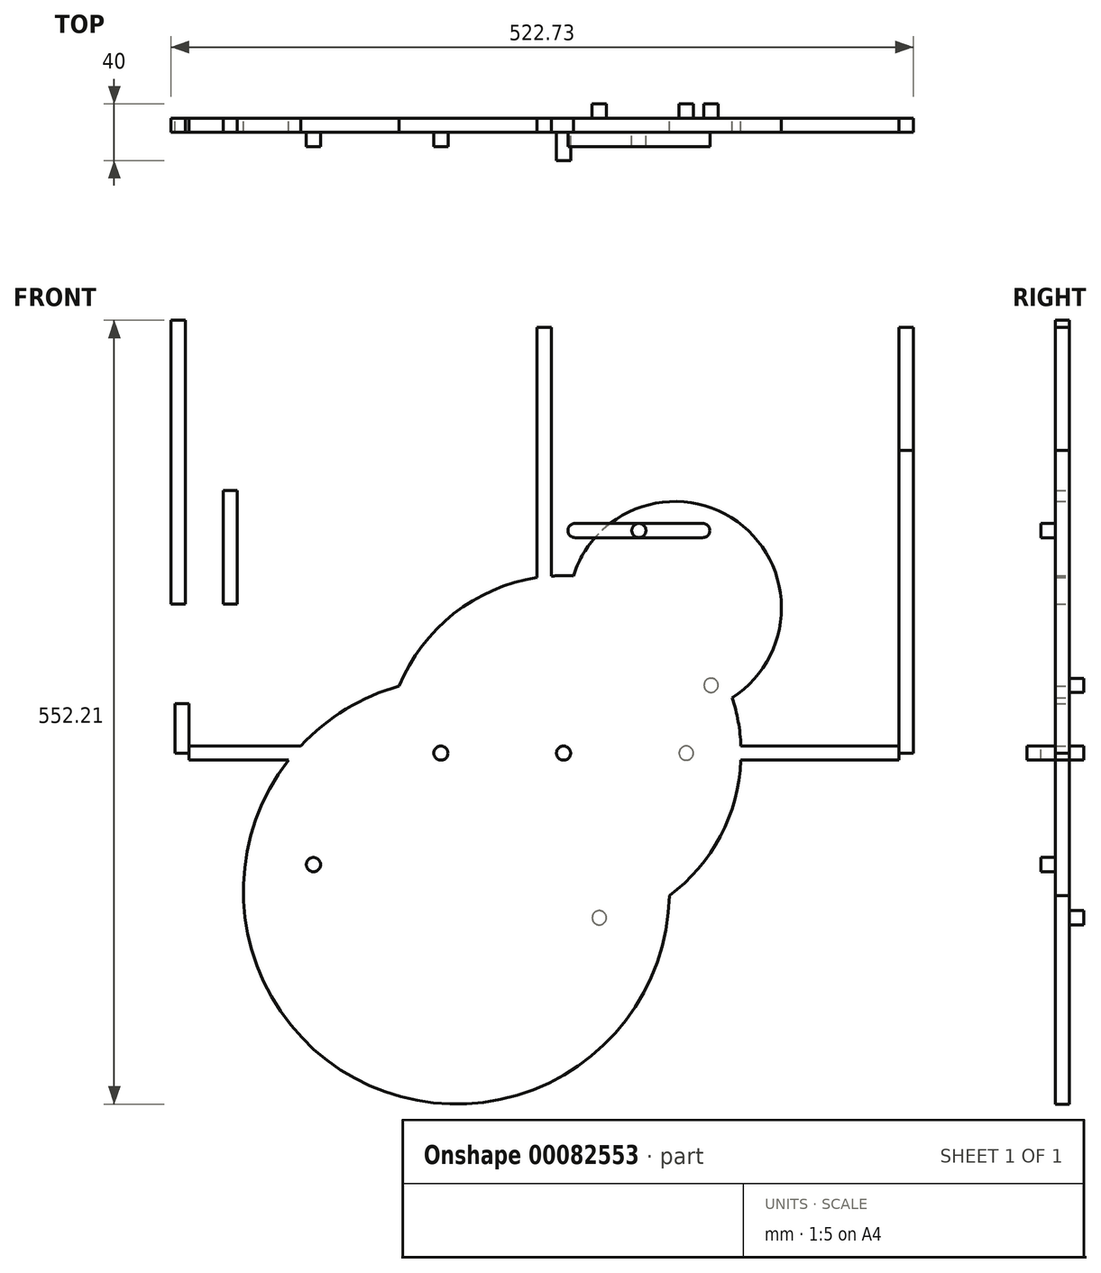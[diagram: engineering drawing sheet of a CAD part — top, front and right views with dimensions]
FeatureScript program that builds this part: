
annotation { "Feature Type Name" : "Feature", "Feature Type Description" : "" }
export const myFeature = defineFeature(function(context is Context, id is Id, definition is map)
    precondition{}
    {
        {
            var Q0;
            Q0=qCreatedBy(makeId("Front.planeOp"),FACE);
            var sketch = newSketch(context, id + "F0", { "sketchPlane" : qUnion([Q0])});
            skLineSegment(sketch, "E0", {"start": v(0, 0) * mm, "end": v(0, -300) * mm, "construction": true});
            skLineSegment(sketch, "E1", {"start": v(0, -300) * mm, "end": v(250, -300) * mm, "construction": true});
            skLineSegment(sketch, "E2", {"start": v(0, -300) * mm, "end": v(-250, -300) * mm, "construction": true});
            skLineSegment(sketch, "E3", {"start": v(0, 0) * mm, "end": v(5, 0) * mm});
            skLineSegment(sketch, "E4", {"start": v(5, 0) * mm, "end": v(5, -295) * mm});
            skLineSegment(sketch, "E5", {"start": v(5, -295) * mm, "end": v(250, -295) * mm});
            skLineSegment(sketch, "E6", {"start": v(250, -295) * mm, "end": v(250, -305) * mm});
            skLineSegment(sketch, "E7", {"start": v(250, -305) * mm, "end": v(-250, -305) * mm});
            skLineSegment(sketch, "E8", {"start": v(-250, -305) * mm, "end": v(-250, -295) * mm});
            skLineSegment(sketch, "E9", {"start": v(-250, -295) * mm, "end": v(-5, -295) * mm});
            skLineSegment(sketch, "E10", {"start": v(-5, -295) * mm, "end": v(-5, 0) * mm});
            skLineSegment(sketch, "E11", {"start": v(-5, 0) * mm, "end": v(0, 0) * mm});
            skSolve(sketch);
        }
        {
            var Q0;
            Q0 = qSketchRegion(id + "F0", true);
            extrude(context, id + "F1", {"entities" : qUnion([Q0]), "depth" : 10 * mm});
        }
        {
            var Q0;
            Q0=qCreatedBy(makeId("Front.planeOp"),FACE);
            var sketch = newSketch(context, id + "F2", { "sketchPlane" : qUnion([Q0])});
            skPoint(sketch, "E12.0", {"position": v(0, 0) * mm});
            skLineSegment(sketch, "E12.1", {"start": v(0, -300) * mm, "end": v(250, -300) * mm, "construction": true});
            skLineSegment(sketch, "E12.2", {"start": v(0, -300) * mm, "end": v(-250, -300) * mm, "construction": true});
            skLineSegment(sketch, "E13", {"start": v(0, 0) * mm, "end": v(0, 50) * mm, "construction": true});
            skLineSegment(sketch, "E14", {"start": v(0, 0) * mm, "end": v(-25.88, 96.6) * mm, "construction": true});
            skLineSegment(sketch, "E15", {"start": v(0, 0) * mm, "end": v(-100, 0) * mm, "construction": true});
            skLineSegment(sketch, "E16", {"start": v(0, 0) * mm, "end": v(-79.7, -6.97) * mm});
            skLineSegment(sketch, "E17", {"start": v(0, 0) * mm, "end": v(20.7, -77.27) * mm});
            skLineSegment(sketch, "E18", {"start": v(0, 0) * mm, "end": v(139.9, -300) * mm, "construction": true});
            skLineSegment(sketch, "E19", {"start": v(20.7, -77.27) * mm, "end": v(117.62, -252.23) * mm, "construction": true});
            skLineSegment(sketch, "E20", {"start": v(-79.7, -6.97) * mm, "end": v(66.76, -143.17) * mm, "construction": true});
            skLineSegment(sketch, "E21", {"start": v(66.76, -143.17) * mm, "end": v(117.62, -252.23) * mm});
            skCircle(sketch, "E22", {"center": v(92.19, -197.7) * mm, "radius": 75 * mm});
            skCircle(sketch, "E23", {"center": v(66.76, -143.17) * mm, "radius": 5 * mm});
            skLineSegment(sketch, "E24", {"start": v(-262.73, 4.92) * mm, "end": v(-262.73, -195.08) * mm});
            skLineSegment(sketch, "E25", {"start": v(-262.73, -195.08) * mm, "end": v(-252.73, -195.08) * mm});
            skLineSegment(sketch, "E26", {"start": v(-252.73, -195.08) * mm, "end": v(-252.73, 4.92) * mm});
            skLineSegment(sketch, "E27", {"start": v(-252.73, 4.92) * mm, "end": v(-262.73, 4.92) * mm});
            skLineSegment(sketch, "E28", {"start": v(92.19, -197.7) * mm, "end": v(87.19, -197.7) * mm});
            skLineSegment(sketch, "E29", {"start": v(87.19, -197.7) * mm, "end": v(87.19, -300) * mm});
            skLineSegment(sketch, "E30", {"start": v(87.19, -300) * mm, "end": v(97.19, -300) * mm});
            skLineSegment(sketch, "E31", {"start": v(97.19, -300) * mm, "end": v(97.19, -197.7) * mm});
            skLineSegment(sketch, "E32", {"start": v(97.19, -197.7) * mm, "end": v(92.19, -197.7) * mm});
            skLineSegment(sketch, "E33", {"start": v(-226.11, -195.08) * mm, "end": v(-226.11, -115.08) * mm});
            skLineSegment(sketch, "E34", {"start": v(-226.11, -115.08) * mm, "end": v(-216.11, -115.08) * mm});
            skLineSegment(sketch, "E35", {"start": v(-216.11, -115.08) * mm, "end": v(-216.11, -195.08) * mm});
            skLineSegment(sketch, "E36", {"start": v(-216.11, -195.08) * mm, "end": v(-226.11, -195.08) * mm});
            skLineSegment(sketch, "E37", {"start": v(97.19, -197.7) * mm, "end": v(132.22, -272.82) * mm});
            skLineSegment(sketch, "E38", {"start": v(132.22, -272.82) * mm, "end": v(128.11, -274.74) * mm});
            skLineSegment(sketch, "E39", {"start": v(124, -276.65) * mm, "end": v(97.19, -219.14) * mm});
            skLineSegment(sketch, "E40", {"start": v(124, -276.65) * mm, "end": v(124, -276.65) * mm});
            skLineSegment(sketch, "E41", {"start": v(128.11, -274.74) * mm, "end": v(124, -276.65) * mm});
            skSolve(sketch);
        }
        {
            var Q0;
            {var subQ1=sQuery(id+"F2.wireOp",EDGE,"E28");Q0=makeQuery(id+"F2.imprint","IMPRINT",FACE,{"disambiguationData":[TD([[makeQuery(id+"F2.imprint","IMPRINT",EDGE,{"derivedFrom":subQ1}),1.0]])]});}
            var Q1;
            {var subQ5=sQuery(id+"F2.wireOp",EDGE,"E30");Q1=makeQuery(id+"F2.imprint","IMPRINT",FACE,{"disambiguationData":[TD([[makeQuery(id+"F2.imprint","IMPRINT",EDGE,{"derivedFrom":subQ5}),1.0]])]});}
            var Q2;
            Q2=makeQuery(id+"F2.imprint","IMPRINT",FACE,{"disambiguationData":[TD([[makeQuery(id+"F2.imprint","IMPRINT",EDGE,{"derivedFrom":sQuery(id+"F2.wireOp",EDGE,"E33")}),-1.0]])]});
            var Q3;
            Q3=makeQuery(id+"F2.imprint","IMPRINT",FACE,{"disambiguationData":[TD([[makeQuery(id+"F2.imprint","IMPRINT",EDGE,{"derivedFrom":sQuery(id+"F2.wireOp",EDGE,"E24")}),1.0]])]});
            var Q4;
            {var subQ0=sQuery(id+"F2.wireOp",EDGE,"E32");Q4=makeQuery(id+"F2.imprint","IMPRINT",FACE,{"disambiguationData":[TD([[makeQuery(id+"F2.imprint","IMPRINT",EDGE,{"derivedFrom":subQ0}),1.0]])]});}
            var Q5;
            {var subQ3=sQuery(id+"F2.wireOp",EDGE,"E22");var subQ6=sQuery(id+"F2.wireOp",EDGE,"E39");var subQ8=makeQuery(id+"F2.imprint","INTERSECT",VERTEX,{"derivedFrom":[subQ3,subQ6]});Q5=makeQuery(id+"F2.imprint","IMPRINT",FACE,{"disambiguationData":[TD([[makeQuery(id+"F2.imprint","IMPRINT",EDGE,{"disambiguationData":[TD([[subQ8,-1.0]])],"derivedFrom":subQ3}),1.0]])]});}
            var Q6;
            {var subQ0=sQuery(id+"F2.wireOp",EDGE,"E38");Q6=makeQuery(id+"F2.imprint","IMPRINT",FACE,{"disambiguationData":[TD([[makeQuery(id+"F2.imprint","IMPRINT",EDGE,{"derivedFrom":subQ0}),-1.0]])]});}
            extrude(context, id + "F3", {"entities" : qUnion([Q0, Q1, Q2, Q3, Q4, Q5, Q6]), "operationType" : NewBodyOperationType.ADD, "depth" : 10 * mm});
        }
        {
            var Q0;
            {var subQ1=sQuery(id+"F2.wireOp",EDGE,"E28");Q0=makeQuery(id+"F2.imprint","IMPRINT",FACE,{"disambiguationData":[TD([[makeQuery(id+"F2.imprint","IMPRINT",EDGE,{"derivedFrom":subQ1}),1.0]])]});}
            var Q1;
            {var subQ0=sQuery(id+"F2.wireOp",EDGE,"E32");Q1=makeQuery(id+"F2.imprint","IMPRINT",FACE,{"disambiguationData":[TD([[makeQuery(id+"F2.imprint","IMPRINT",EDGE,{"derivedFrom":subQ0}),1.0]])]});}
            var Q2;
            Q2=makeQuery(id+"F2.imprint","IMPRINT",FACE,{"disambiguationData":[TD([[makeQuery(id+"F2.imprint","IMPRINT",EDGE,{"derivedFrom":sQuery(id+"F2.wireOp",EDGE,"E23")}),-1.0]])]});
            var Q3;
            {var subQ0=sQuery(id+"F2.wireOp",EDGE,"E31");var subQ1=sQuery(id+"F2.wireOp",EDGE,"E22");var subQ2=makeQuery(id+"F2.imprint","INTERSECT",VERTEX,{"derivedFrom":[subQ1,subQ0]});Q3=makeQuery(id+"F2.imprint","IMPRINT",FACE,{"disambiguationData":[TD([[makeQuery(id+"F2.imprint","IMPRINT",EDGE,{"disambiguationData":[TD([[subQ2,-1.0]])],"derivedFrom":subQ1}),1.0]])]});}
            var Q4;
            {var subQ3=sQuery(id+"F2.wireOp",EDGE,"E22");var subQ6=sQuery(id+"F2.wireOp",EDGE,"E39");var subQ8=makeQuery(id+"F2.imprint","INTERSECT",VERTEX,{"derivedFrom":[subQ3,subQ6]});Q4=makeQuery(id+"F2.imprint","IMPRINT",FACE,{"disambiguationData":[TD([[makeQuery(id+"F2.imprint","IMPRINT",EDGE,{"disambiguationData":[TD([[subQ8,-1.0]])],"derivedFrom":subQ3}),1.0]])]});}
            extrude(context, id + "F4", {"entities" : qUnion([Q0, Q1, Q2, Q3, Q4]), "depth" : 10 * mm});
        }
        {
            var Q0;
            Q0=makeQuery(id+"F2.imprint","IMPRINT",FACE,{"disambiguationData":[TD([[makeQuery(id+"F2.imprint","IMPRINT",EDGE,{"derivedFrom":sQuery(id+"F2.wireOp",EDGE,"E23")}),1.0]])]});
            extrude(context, id + "F5", {"entities" : qUnion([Q0]), "operationType" : NewBodyOperationType.ADD, "depth" : 20 * mm});
        }
        {
            var Q0;
            Q0=makeQuery(id+"F4.opExtrude","CAP_FACE",FACE,{"disambiguationData":[OSD([sQuery(id+"F2.wireOp",EDGE,"E22"),sQuery(id+"F2.wireOp",EDGE,"E23")])],"isStart":false});
            var sketch = newSketch(context, id + "F6", { "sketchPlane" : qUnion([Q0])});
            skCircle(sketch, "E42.0", {"center": v(66.76, -143.17) * mm, "radius": 5 * mm});
            skLineSegment(sketch, "E43", {"start": v(66.76, -138.17) * mm, "end": v(111.76, -138.17) * mm});
            skLineSegment(sketch, "E44", {"start": v(66.76, -138.17) * mm, "end": v(21.76, -138.17) * mm});
            skLineSegment(sketch, "E45", {"start": v(16.76, -143.17) * mm, "end": v(16.76, -143.17) * mm});
            skLineSegment(sketch, "E46", {"start": v(21.76, -148.17) * mm, "end": v(66.76, -148.17) * mm});
            skLineSegment(sketch, "E47", {"start": v(66.76, -148.17) * mm, "end": v(111.76, -148.17) * mm});
            skLineSegment(sketch, "E48", {"start": v(116.76, -143.17) * mm, "end": v(116.76, -143.17) * mm});
            skPoint(sketch, "E49.visualSharp", {"position": v(16.76, -138.17) * mm});
            skArc(sketch, "E49.filletArc", {"start": v(21.76, -138.17) * mm, "mid": v(18.23, -139.64) * mm, "end": v(16.76, -143.17) * mm});
            skPoint(sketch, "E50.visualSharp", {"position": v(16.76, -148.17) * mm});
            skArc(sketch, "E50.filletArc", {"start": v(16.76, -143.17) * mm, "mid": v(18.23, -146.7) * mm, "end": v(21.76, -148.17) * mm});
            skPoint(sketch, "E51.visualSharp", {"position": v(116.76, -148.17) * mm});
            skArc(sketch, "E51.filletArc", {"start": v(111.76, -148.17) * mm, "mid": v(115.3, -146.7) * mm, "end": v(116.76, -143.17) * mm});
            skPoint(sketch, "E52.visualSharp", {"position": v(116.76, -138.17) * mm});
            skArc(sketch, "E52.filletArc", {"start": v(116.76, -143.17) * mm, "mid": v(115.3, -139.64) * mm, "end": v(111.76, -138.17) * mm});
            skSolve(sketch);
        }
        {
            var Q0;
            {var subQ1=sQuery(id+"F6.wireOp",EDGE,"E49.filletArc");Q0=makeQuery(id+"F6.imprint","IMPRINT",FACE,{"disambiguationData":[TD([[makeQuery(id+"F6.imprint","IMPRINT",EDGE,{"derivedFrom":subQ1}),1.0]])]});}
            var Q1;
            {var subQ1=sQuery(id+"F6.wireOp",EDGE,"E43");Q1=makeQuery(id+"F6.imprint","IMPRINT",FACE,{"disambiguationData":[TD([[makeQuery(id+"F6.imprint","IMPRINT",EDGE,{"derivedFrom":subQ1}),-1.0]])]});}
            var Q2;
            {var subQ0=sQuery(id+"F6.wireOp",EDGE,"E44");var subQ5=makeQuery(id+"F4.opExtrude","CAP_EDGE",EDGE,{"disambiguationData":[OSD([sQuery(id+"F2.wireOp",EDGE,"E22")])],"isStart":false});var subQ6=makeQuery(id+"F6.imprint","INTERSECT",VERTEX,{"derivedFrom":[subQ5,subQ0]});Q2=makeQuery(id+"F6.imprint","IMPRINT",FACE,{"disambiguationData":[TD([[makeQuery(id+"F6.imprint","IMPRINT",EDGE,{"disambiguationData":[TD([[subQ6,-1.0]])],"derivedFrom":subQ5}),1.0]])]});}
            var Q3;
            {var subQ0=sQuery(id+"F6.wireOp",EDGE,"E42.0");var subQ1=makeQuery(id+"F6.imprint","INTERSECT",VERTEX,{"derivedFrom":[subQ0,sQuery(id+"F6.wireOp",EDGE,"E43"),sQuery(id+"F6.wireOp",EDGE,"E44")]});Q3=makeQuery(id+"F6.imprint","IMPRINT",FACE,{"disambiguationData":[TD([[makeQuery(id+"F6.imprint","IMPRINT",EDGE,{"disambiguationData":[TD([[subQ1,-1.0]])],"derivedFrom":subQ0}),1.0]])]});}
            extrude(context, id + "F7", {"entities" : qUnion([Q0, Q1, Q2, Q3]), "depth" : 10 * mm});
        }
        {
            var Q0;
            Q0=qCreatedBy(makeId("Front.planeOp"),FACE);
            var sketch = newSketch(context, id + "F8", { "sketchPlane" : qUnion([Q0])});
            skPoint(sketch, "E53.2", {"position": v(0, 0) * mm});
            skLineSegment(sketch, "E53.3", {"start": v(0, -300) * mm, "end": v(-250, -300) * mm, "construction": true});
            skLineSegment(sketch, "E53.4", {"start": v(0, -300) * mm, "end": v(250, -300) * mm, "construction": true});
            skLineSegment(sketch, "E54.0", {"start": v(0, 0) * mm, "end": v(20.7, -77.27) * mm});
            skLineSegment(sketch, "E54.1", {"start": v(0, 0) * mm, "end": v(-79.7, -6.97) * mm});
            skLineSegment(sketch, "E55", {"start": v(20.7, -77.27) * mm, "end": v(100.15, -86.67) * mm});
            skLineSegment(sketch, "E56", {"start": v(-72.72, -86.67) * mm, "end": v(100.15, -86.67) * mm, "construction": true});
            skLineSegment(sketch, "E57", {"start": v(100.15, -86.67) * mm, "end": v(100.15, -300) * mm, "construction": true});
            skCircle(sketch, "E58", {"center": v(13.71, -300) * mm, "radius": 125 * mm});
            skCircle(sketch, "E59", {"center": v(-72.72, -300) * mm, "radius": 5 * mm});
            skCircle(sketch, "E60", {"center": v(13.71, -300) * mm, "radius": 5 * mm});
            skLineSegment(sketch, "E61", {"start": v(260, -86.67) * mm, "end": v(260, -300) * mm});
            skLineSegment(sketch, "E62", {"start": v(260, -300) * mm, "end": v(250, -300) * mm});
            skLineSegment(sketch, "E63", {"start": v(-79.7, -6.97) * mm, "end": v(-79.7, 43.03) * mm, "construction": true});
            skLineSegment(sketch, "E64", {"start": v(-79.7, -6.97) * mm, "end": v(-72.72, -86.67) * mm});
            skLineSegment(sketch, "E65", {"start": v(-72.72, -86.67) * mm, "end": v(-72.72, -300) * mm});
            skLineSegment(sketch, "E66", {"start": v(13.71, -86.67) * mm, "end": v(13.71, -300) * mm, "construction": true});
            skLineSegment(sketch, "E67", {"start": v(250, -300) * mm, "end": v(250, -86.67) * mm});
            skLineSegment(sketch, "E68", {"start": v(250, -86.67) * mm, "end": v(260, -86.67) * mm});
            skSolve(sketch);
        }
        {
            var Q0;
            Q0=makeQuery(id+"F8.imprint","IMPRINT",FACE,{"disambiguationData":[TD([[makeQuery(id+"F8.imprint","IMPRINT",EDGE,{"derivedFrom":sQuery(id+"F8.wireOp",EDGE,"E58")}),1.0]])]});
            var Q1;
            Q1=makeQuery(id+"F8.imprint","IMPRINT",FACE,{"disambiguationData":[TD([[makeQuery(id+"F8.imprint","IMPRINT",EDGE,{"derivedFrom":sQuery(id+"F8.wireOp",EDGE,"E60")}),1.0]])]});
            var Q2;
            Q2=makeQuery(id+"F8.imprint","IMPRINT",FACE,{"disambiguationData":[TD([[makeQuery(id+"F8.imprint","IMPRINT",EDGE,{"derivedFrom":sQuery(id+"F8.wireOp",EDGE,"E61")}),-1.0]])]});
            extrude(context, id + "F9", {"entities" : qUnion([Q0, Q1, Q2]), "depth" : 10 * mm});
        }
        {
            var Q0;
            Q0=makeQuery(id+"F8.imprint","IMPRINT",FACE,{"disambiguationData":[TD([[makeQuery(id+"F8.imprint","IMPRINT",EDGE,{"derivedFrom":sQuery(id+"F8.wireOp",EDGE,"E59")}),1.0]])]});
            extrude(context, id + "F10", {"entities" : qUnion([Q0]), "operationType" : NewBodyOperationType.ADD, "depth" : 20 * mm});
        }
        {
            var Q0;
            Q0=makeQuery(id+"F8.imprint","IMPRINT",FACE,{"disambiguationData":[TD([[makeQuery(id+"F8.imprint","IMPRINT",EDGE,{"derivedFrom":sQuery(id+"F8.wireOp",EDGE,"E60")}),1.0]])]});
            extrude(context, id + "F11", {"entities" : qUnion([Q0]), "operationType" : NewBodyOperationType.ADD, "depth" : 30 * mm});
        }
        {
            var Q0;
            Q0=qCreatedBy(makeId("Front.planeOp"),FACE);
            var sketch = newSketch(context, id + "F12", { "sketchPlane" : qUnion([Q0])});
            skLineSegment(sketch, "E69.0", {"start": v(0, -300) * mm, "end": v(-250, -300) * mm, "construction": true});
            skLineSegment(sketch, "E69.1", {"start": v(0, -300) * mm, "end": v(250, -300) * mm, "construction": true});
            skLineSegment(sketch, "E69.3", {"start": v(0, 0) * mm, "end": v(-79.7, -6.97) * mm, "construction": true});
            skLineSegment(sketch, "E69.4", {"start": v(0, 0) * mm, "end": v(20.7, -77.27) * mm, "construction": true});
            skLineSegment(sketch, "E69.5", {"start": v(20.7, -77.27) * mm, "end": v(100.15, -86.67) * mm, "construction": true});
            skLineSegment(sketch, "E70", {"start": v(-72.72, -86.67) * mm, "end": v(-107.59, -83.62) * mm});
            skLineSegment(sketch, "E71", {"start": v(100.15, -86.67) * mm, "end": v(93.75, -121.08) * mm});
            skLineSegment(sketch, "E72", {"start": v(-107.59, -83.62) * mm, "end": v(93.75, -121.08) * mm, "construction": true});
            skLineSegment(sketch, "E73", {"start": v(-6.92, -102.35) * mm, "end": v(-61.8, -397.29) * mm, "construction": true});
            skLineSegment(sketch, "E74", {"start": v(-107.59, -83.62) * mm, "end": v(-162.46, -378.56) * mm, "construction": true});
            skLineSegment(sketch, "E75", {"start": v(93.75, -121.08) * mm, "end": v(38.88, -416.02) * mm, "construction": true});
            skCircle(sketch, "E76", {"center": v(-61.8, -397.29) * mm, "radius": 150 * mm});
            skCircle(sketch, "E77", {"center": v(-162.46, -378.56) * mm, "radius": 5 * mm});
            skLineSegment(sketch, "E78", {"start": v(-61.8, -397.29) * mm, "end": v(-56.88, -398.2) * mm});
            skLineSegment(sketch, "E79", {"start": v(-56.88, -398.2) * mm, "end": v(-38.6, -300) * mm});
            skLineSegment(sketch, "E80", {"start": v(-38.6, -300) * mm, "end": v(-48.78, -300) * mm});
            skLineSegment(sketch, "E81", {"start": v(-48.78, -300) * mm, "end": v(-66.7, -396.37) * mm});
            skLineSegment(sketch, "E82", {"start": v(-66.7, -396.37) * mm, "end": v(-61.8, -397.29) * mm});
            skLineSegment(sketch, "E83", {"start": v(250, -300) * mm, "end": v(250, 0) * mm});
            skLineSegment(sketch, "E84", {"start": v(250, 0) * mm, "end": v(260, 0) * mm});
            skLineSegment(sketch, "E85", {"start": v(260, 0) * mm, "end": v(260, -300) * mm});
            skLineSegment(sketch, "E86", {"start": v(260, -300) * mm, "end": v(250, -300) * mm});
            skLineSegment(sketch, "E87", {"start": v(-250, -300) * mm, "end": v(-250, -265) * mm});
            skLineSegment(sketch, "E88", {"start": v(-250, -265) * mm, "end": v(-260, -265) * mm});
            skLineSegment(sketch, "E89", {"start": v(-260, -265) * mm, "end": v(-260, -300) * mm});
            skLineSegment(sketch, "E90", {"start": v(-260, -300) * mm, "end": v(-250, -300) * mm});
            skLineSegment(sketch, "E91.0", {"start": v(-79.7, -6.97) * mm, "end": v(-72.72, -86.67) * mm, "construction": true});
            skSolve(sketch);
        }
        {
            var Q0;
            Q0=makeQuery(id+"F12.imprint","IMPRINT",FACE,{"disambiguationData":[TD([[makeQuery(id+"F12.imprint","IMPRINT",EDGE,{"derivedFrom":sQuery(id+"F12.wireOp",EDGE,"E87")}),1.0]])]});
            var Q1;
            Q1=makeQuery(id+"F12.imprint","IMPRINT",FACE,{"disambiguationData":[TD([[makeQuery(id+"F12.imprint","IMPRINT",EDGE,{"derivedFrom":sQuery(id+"F12.wireOp",EDGE,"E76")}),1.0]])]});
            var Q2;
            Q2=makeQuery(id+"F12.imprint","IMPRINT",FACE,{"disambiguationData":[TD([[makeQuery(id+"F12.imprint","IMPRINT",EDGE,{"derivedFrom":sQuery(id+"F12.wireOp",EDGE,"E78")}),1.0]])]});
            var Q3;
            Q3=makeQuery(id+"F12.imprint","IMPRINT",FACE,{"disambiguationData":[TD([[makeQuery(id+"F12.imprint","IMPRINT",EDGE,{"derivedFrom":sQuery(id+"F12.wireOp",EDGE,"E83")}),-1.0]])]});
            extrude(context, id + "F13", {"entities" : qUnion([Q0, Q1, Q2, Q3]), "depth" : 10 * mm});
        }
        {
            var Q0;
            Q0=makeQuery(id+"F12.imprint","IMPRINT",FACE,{"disambiguationData":[TD([[makeQuery(id+"F12.imprint","IMPRINT",EDGE,{"derivedFrom":sQuery(id+"F12.wireOp",EDGE,"E77")}),1.0]])]});
            extrude(context, id + "F14", {"entities" : qUnion([Q0]), "operationType" : NewBodyOperationType.ADD, "depth" : 20 * mm});
        }
        {
            var Q0;
            Q0=makeQuery(id+"F12.imprint","IMPRINT",FACE,{"disambiguationData":[TD([[makeQuery(id+"F12.imprint","IMPRINT",EDGE,{"derivedFrom":sQuery(id+"F12.wireOp",EDGE,"E78")}),1.0]])]});
            extrude(context, id + "F15", {"entities" : qUnion([Q0]), "operationType" : NewBodyOperationType.ADD, "depth" : 10 * mm});
        }
        {
            var Q0;
            {var subQ0=sQuery(id+"F12.wireOp",EDGE,"E77");Q0=makeQuery(id+"F14.boolean.opBoolean","MERGE",FACE,{"derivedFrom":[makeQuery(id+"F13.opExtrude","CAP_FACE",FACE,{"disambiguationData":[OSD([sQuery(id+"F12.wireOp",EDGE,"E76"),subQ0])],"isStart":true}),makeQuery(id+"F14.opExtrude","CAP_FACE",FACE,{"disambiguationData":[OSD([subQ0])],"isStart":true})]});}
            var sketch = newSketch(context, id + "F16", { "sketchPlane" : qUnion([Q0])});
            skPoint(sketch, "E92.0", {"position": v(-117.62, -252.23) * mm});
            skCircle(sketch, "E92.1", {"center": v(-66.76, -143.17) * mm, "radius": 5 * mm, "construction": true});
            skPoint(sketch, "E93.0", {"position": v(-100.12, -300) * mm});
            skPoint(sketch, "E94.0", {"position": v(-38.88, -416.02) * mm});
            skCircle(sketch, "E95", {"center": v(-117.62, -252.23) * mm, "radius": 5 * mm});
            skCircle(sketch, "E96", {"center": v(-100.12, -300) * mm, "radius": 5 * mm});
            skCircle(sketch, "E97", {"center": v(-38.88, -416.02) * mm, "radius": 5 * mm});
            skSolve(sketch);
        }
        {
            var Q0;
            Q0=makeQuery(id+"F16.imprint","IMPRINT",FACE,{"disambiguationData":[TD([[makeQuery(id+"F16.imprint","IMPRINT",EDGE,{"derivedFrom":sQuery(id+"F16.wireOp",EDGE,"E95")}),1.0]])]});
            extrude(context, id + "F17", {"entities" : qUnion([Q0]), "operationType" : NewBodyOperationType.ADD, "depth" : 10 * mm});
        }
        {
            var Q0;
            Q0=makeQuery(id+"F16.imprint","IMPRINT",FACE,{"disambiguationData":[TD([[makeQuery(id+"F16.imprint","IMPRINT",EDGE,{"derivedFrom":sQuery(id+"F16.wireOp",EDGE,"E96")}),1.0]])]});
            extrude(context, id + "F18", {"entities" : qUnion([Q0]), "operationType" : NewBodyOperationType.ADD, "depth" : 10 * mm});
        }
        {
            var Q0;
            Q0=makeQuery(id+"F16.imprint","IMPRINT",FACE,{"disambiguationData":[TD([[makeQuery(id+"F16.imprint","IMPRINT",EDGE,{"derivedFrom":sQuery(id+"F16.wireOp",EDGE,"E97")}),1.0]])]});
            extrude(context, id + "F19", {"entities" : qUnion([Q0]), "operationType" : NewBodyOperationType.ADD, "depth" : 10 * mm});
        }
    });
